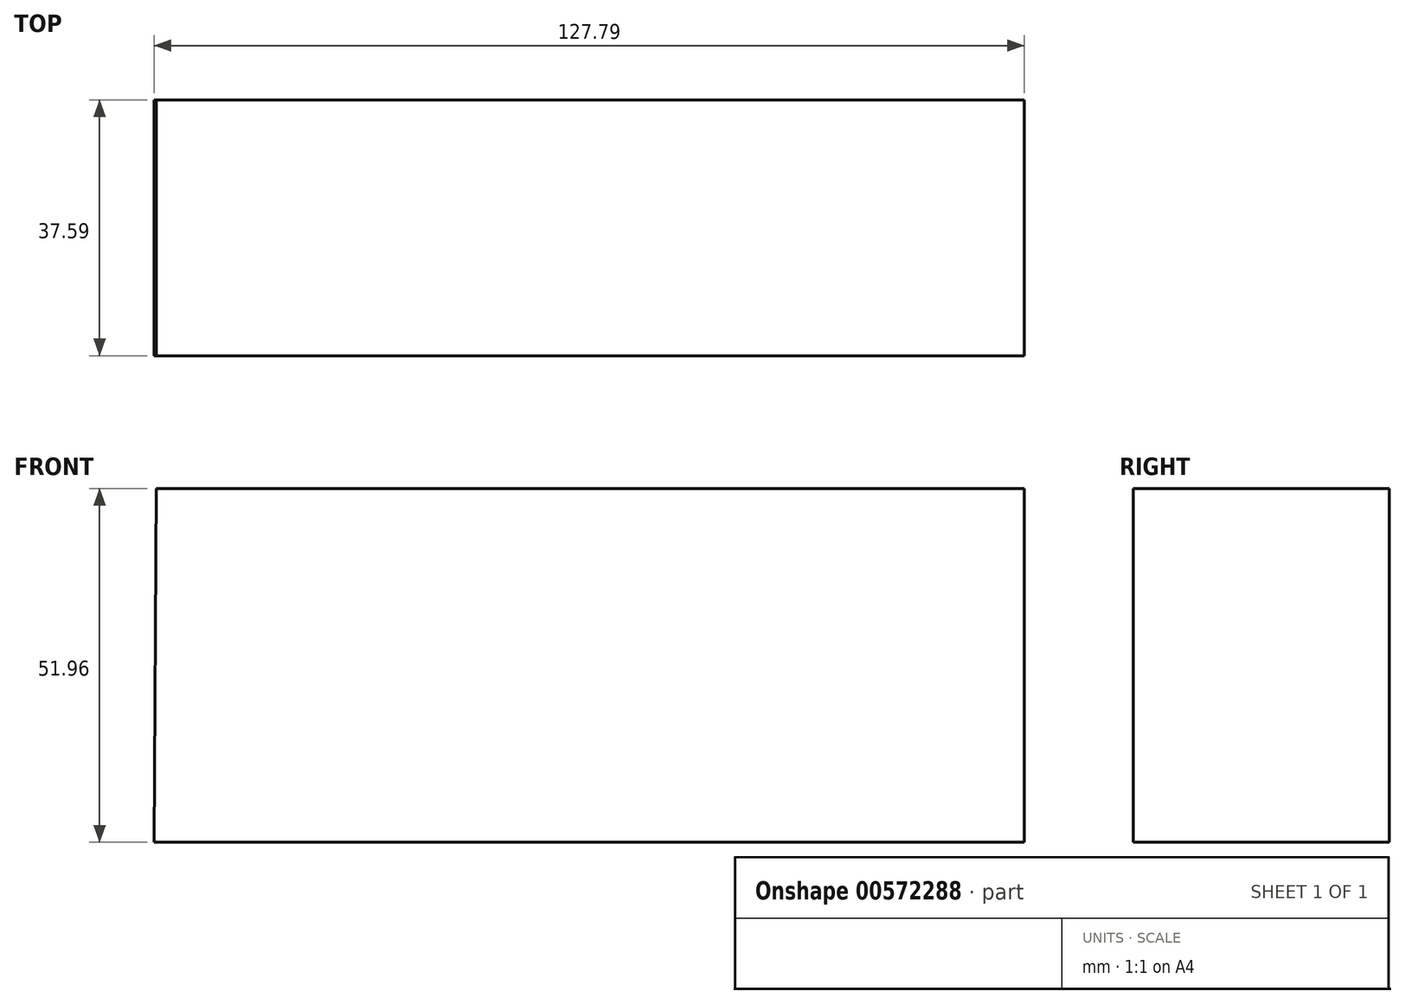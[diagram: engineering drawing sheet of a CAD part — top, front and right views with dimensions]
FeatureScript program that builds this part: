
annotation { "Feature Type Name" : "Feature", "Feature Type Description" : "" }
export const myFeature = defineFeature(function(context is Context, id is Id, definition is map)
    precondition{}
    {
        {
            var Q0;
            Q0=qCreatedBy(makeId("Front.planeOp"),FACE);
            var sketch = newSketch(context, id + "F0", { "sketchPlane" : qUnion([Q0])});
            skLineSegment(sketch, "E0", {"start": v(-51.48, 44.8) * mm, "end": v(76.02, 44.8) * mm});
            skLineSegment(sketch, "E1", {"start": v(76.02, 44.8) * mm, "end": v(76.02, -7.16) * mm});
            skLineSegment(sketch, "E2", {"start": v(76.02, -7.16) * mm, "end": v(-51.77, -7.16) * mm});
            skLineSegment(sketch, "E3", {"start": v(-51.77, -7.16) * mm, "end": v(-51.48, 44.8) * mm});
            skSolve(sketch);
        }
        {
            var Q0;
            Q0=makeQuery(id+"F0.imprint","IMPRINT",FACE,{"disambiguationData":[TD([[makeQuery(id+"F0.imprint","IMPRINT",EDGE,{"derivedFrom":sQuery(id+"F0.wireOp",EDGE,"E0")}),-1.0]])]});
            extrude(context, id + "F1", {"entities" : qUnion([Q0]), "depth" : 37.6 * mm, "offsetDistance" : 25.4 * mm});
        }
    });
